# Revit family: EU_OD-Single-Glass
name_source: partatom
category: Doors
revit_build: Autodesk Revit 2014 (Build: 20130308_1515(x64)
units: mm (PartAtom-declared; Revit-internal decimal feet)

## types (3) — shared parameters
Doorleaf = EU_General Wood
Doorleaf Dim Bottom = 400 mm  [stored 1.31234 ft]
Doorleaf Dim Left = 100 mm  [stored 0.328084 ft]
Doorleaf Dim Right = 100 mm  [stored 0.328084 ft]
Doorleaf Dim Top = 100 mm  [stored 0.328084 ft]
Doorleaf Thickness = 55 mm  [stored 0.180446 ft]
Doornob = EU_Steel
Frame = EU_General Wood
Frame Depth = 100 mm  [stored 0.328084 ft]
Frame Thickness = 40 mm  [stored 0.131234 ft]
Function = Interior
Glass = EU_Glass
Wall Closure = By host

## per-type parameters (varying)
| type | Height | Rough Height | Rough Width | Treshold | Type Name (in Project) | Width |
| 10x21 | 2110 mm  [stored 6.92257 ft] | 21 mm | 10 mm  [stored 0.0328084 ft] | EU_Frame | Type name | 1010 mm  [stored 3.31365 ft] |
| 9x21 | 2110 mm  [stored 6.92257 ft] | 21 mm | 9 mm  [stored 0.0295276 ft] | EU_General Wood | Sett inn typenr (D1) | 910 mm  [stored 2.98556 ft] |
| 9x24 | 2420 mm  [stored 7.93963 ft] | 24 mm | 9 mm  [stored 0.0295276 ft] | EU_Frame | YD2 | 920 mm  [stored 3.01837 ft] |

note: [stored X ft] marks values corroborated as IEEE doubles in the binary element streams (Revit-internal decimal feet)

## geometry (parser evidence)
native form markers: Sweep x1
no freeform markers — native parametric forms only
